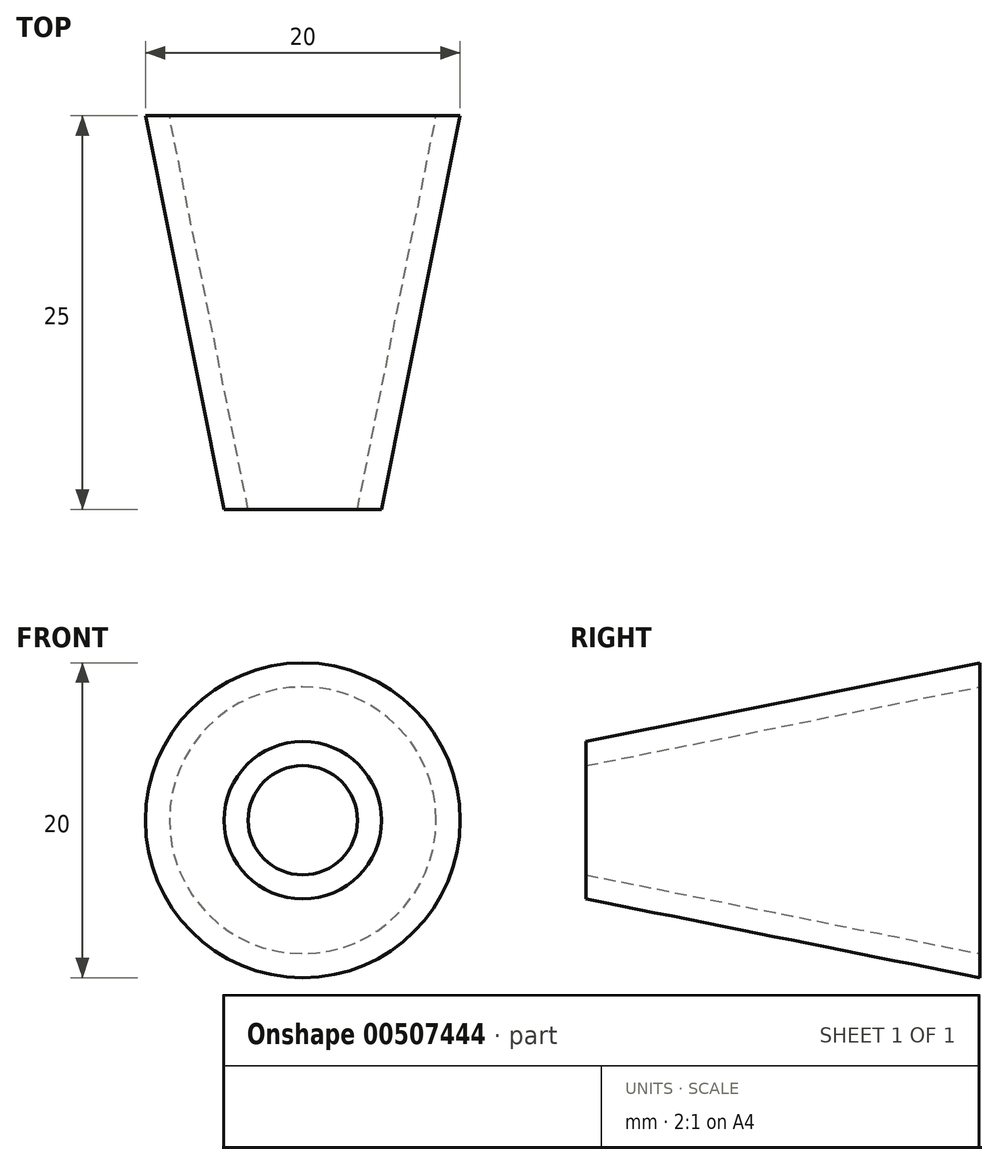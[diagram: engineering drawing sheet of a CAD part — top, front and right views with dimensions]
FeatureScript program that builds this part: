
annotation { "Feature Type Name" : "Feature", "Feature Type Description" : "" }
export const myFeature = defineFeature(function(context is Context, id is Id, definition is map)
    precondition{}
    {
        {
            var Q0;
            Q0=qCreatedBy(makeId("Front.planeOp"),FACE);
            var sketch = newSketch(context, id + "F0", { "sketchPlane" : qUnion([Q0])});
            skCircle(sketch, "E0", {"center": v(0, 0) * mm, "radius": 10 * mm});
            skSolve(sketch);
        }
        {
            var Q0;
            Q0=makeQuery(id+"F0.imprint","IMPRINT",FACE,{"disambiguationData":[TD([[makeQuery(id+"F0.imprint","IMPRINT",EDGE,{"derivedFrom":sQuery(id+"F0.wireOp",EDGE,"E0")}),1.0]])]});
            extrude(context, id + "F1", {"entities" : qUnion([Q0]), "depth" : 25 * mm});
        }
        {
            var Q0;
            Q0=makeQuery(id+"F1.opExtrude","CAP_FACE",FACE,{"disambiguationData":[OSD([sQuery(id+"F0.wireOp",EDGE,"E0")])],"isStart":false});
            var sketch = newSketch(context, id + "F2", { "sketchPlane" : qUnion([Q0])});
            skCircle(sketch, "E1", {"center": v(0, 0) * mm, "radius": 5 * mm});
            skSolve(sketch);
        }
        {
            var Q1;
            Q1=makeQuery(id+"F1.opExtrude","CAP_FACE",FACE,{"disambiguationData":[OSD([sQuery(id+"F0.wireOp",EDGE,"E0")])],"isStart":true});
            var Q2;
            Q2=makeQuery(id+"F2.imprint","IMPRINT",FACE,{"disambiguationData":[TD([[makeQuery(id+"F2.imprint","IMPRINT",EDGE,{"derivedFrom":sQuery(id+"F2.wireOp",EDGE,"E1")}),1.0]])]});
            loft(context, id + "F3", {"operationType" : NewBodyOperationType.INTERSECT, "sheetProfilesArray" : [{ "sheetProfileEntities" : qUnion([Q1]) }, { "sheetProfileEntities" : qUnion([Q2]) }]});
        }
        {
            var Q0;
            Q0=makeQuery(id+"F1.opExtrude","CAP_FACE",FACE,{"disambiguationData":[OSD([sQuery(id+"F0.wireOp",EDGE,"E0")])],"isStart":true});
            var Q1;
            Q1=makeQuery(id+"F1.opExtrude","CAP_FACE",FACE,{"disambiguationData":[OSD([sQuery(id+"F0.wireOp",EDGE,"E0")])],"isStart":false});
            shell(context, id + "F4", {"entities" : qUnion([Q0, Q1]), "thickness" : 1.5 * mm});
        }
    });
